# Revit family: Drinking_Fountain-Acorn-Secure-Care-LR1672FA
name_source: partatom
category: Plumbing Fixtures
units: mm (PartAtom-declared; Revit-internal decimal feet)

## family parameters
Cut with Voids When Loaded = No
Host = Face
OmniClass Number = 23.65.70.14.11
OmniClass Title = Drinking Fountains/Coolers
Part Type = Normal
Room Calculation Point = No
Round Connector Dimension = Use Diameter
Shared = Yes

## types (1)
- LR1672FA-1-03
    -LWE Lavy Waste Extension (3" Standard), Specify Length Beyond Fixture = No
    -TF Transformer, 120VAC to 24VAC (-MVC option only) = No
    03 Single Temp, Non-Metering = Yes
    1 - Off-Floor, Wall Outlet = Yes
    ADA Compliant = Yes
    Assembly Code = D2010810
    BRS - Brass Body Valve = No
    Bowl Shape = Hexagon
    CW Connection = No
    CWFU = 1.5
    Compliance Certifications = Unit shall conform with ANSI, UFAS and ADA 2010 requirements for accessibility
    Default Elevation = 33"
    Description = Secur-Care® Ligature-Resistant, ADA Complaint, Front Access Stainless Steel Trapezoidial Security Drinking Fountain with Hexagonal Bowl
    EG - Enviro-Glaze Color = No
    EVS1 - Electronic Valve System - Single Temp = No
    EVSP1 - Electronic Valve System w/ Piezo Pushbutton = No
    FMT - Fixture Mounted Trim = No
    Finish = Stainless Steel-Acorn-Polished Satin
    Flow Rate = 0.7 GPM
    HW Connection = No
    HWFU = 1.5
    Height = 4 5/8"
    Inlet Diameter Connection = 1/2"
    Length = 18"
    MT - Metal Template (only 1 reqd per project) = No
    MTP1 - Single Temp = No
    MTPP1 - Single Temp, Piezo Button = No
    MVC1 - Time-Trol - Single Temp = No
    MVC1-BAT - Time-Trol - Single Temp - Battery Operation = No
    Manufacturer = Acorn Engineering
    Material = Stainless Steel-Acorn-Polished Satin
    Model = LR1672FA-1-03
    PFB - Power Failure Bypass (Provides drinking water in the event of power failure) = No
    PPZ1 - Programmable Piezo Pushbutton (Single Temperature Only) = No
    Product Documentation Link = https://www.acorneng.com
    Product Page URL = https://www.acorneng.com
    SW - Wall Sleeve = No
    TG - 12 Gage Cabinet = No
    URL = http://www.acorneng.com
    VAC - AcornVac System = No
    Vent Connection = No
    WFU = 2
    Waste Connection = Yes
    Waste Connection Diameter = 1 1/2"
    Width = 21"

## geometry (parser evidence)
native form markers: Sweep x2
no freeform markers — native parametric forms only
